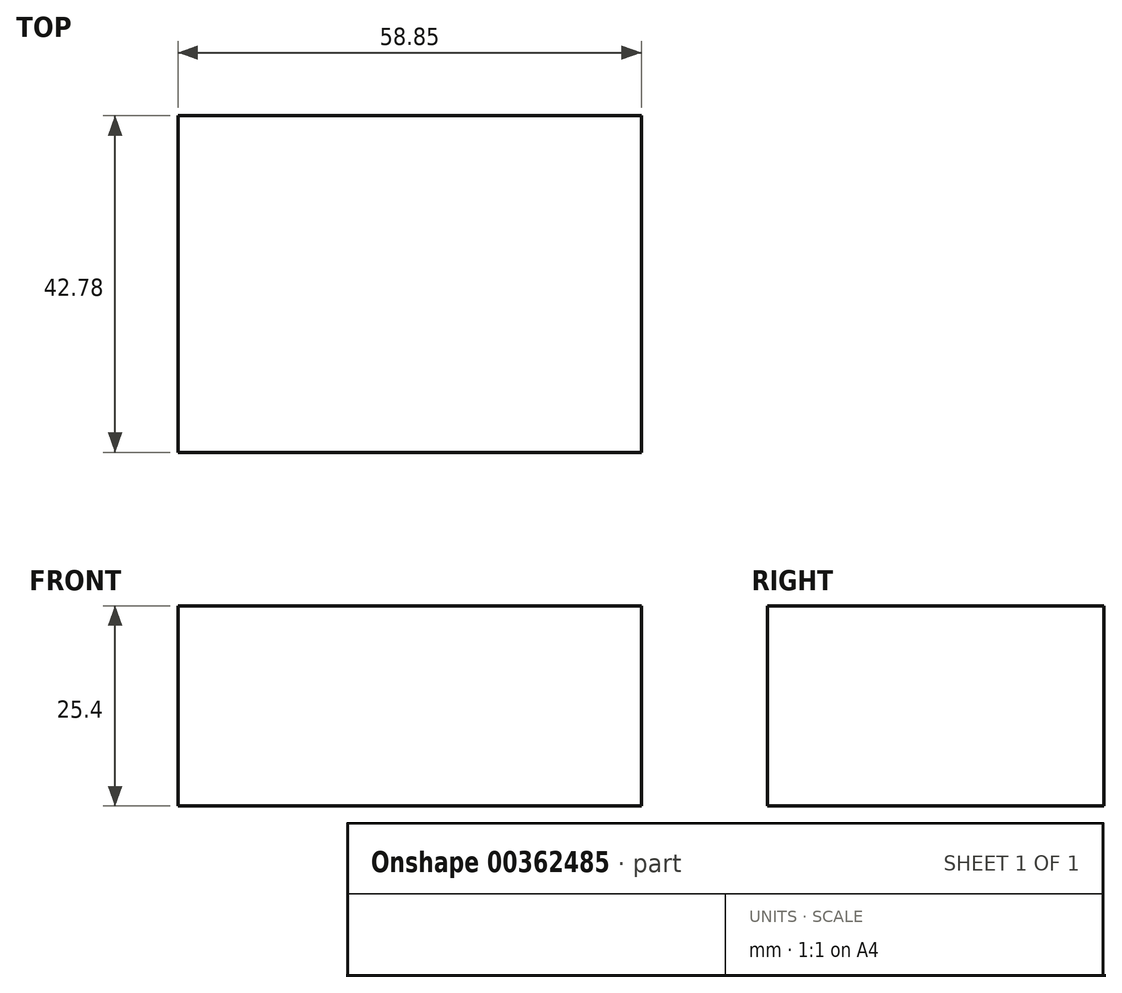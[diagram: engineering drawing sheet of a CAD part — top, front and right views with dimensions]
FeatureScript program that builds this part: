
annotation { "Feature Type Name" : "Feature", "Feature Type Description" : "" }
export const myFeature = defineFeature(function(context is Context, id is Id, definition is map)
    precondition{}
    {
        {
            var Q0;
            Q0=qCreatedBy(makeId("Top.planeOp"),FACE);
            var sketch = newSketch(context, id + "F0", { "sketchPlane" : qUnion([Q0])});
            skLineSegment(sketch, "E0.bottom", {"start": v(64.18, 13.52) * mm, "end": v(5.33, 13.52) * mm});
            skLineSegment(sketch, "E0.top", {"start": v(64.18, 56.3) * mm, "end": v(5.33, 56.3) * mm});
            skLineSegment(sketch, "E0.left", {"start": v(64.18, 13.52) * mm, "end": v(64.18, 56.3) * mm});
            skLineSegment(sketch, "E0.right", {"start": v(5.33, 13.52) * mm, "end": v(5.33, 56.3) * mm});
            skPoint(sketch, "E0.middle", {"position": v(34.75, 34.9) * mm});
            skSolve(sketch);
        }
        {
            var Q0;
            Q0=makeQuery(id+"F0.imprint","IMPRINT",FACE,{"disambiguationData":[TD([[makeQuery(id+"F0.imprint","IMPRINT",EDGE,{"derivedFrom":sQuery(id+"F0.wireOp",EDGE,"E0.bottom")}),-1.0]])]});
            extrude(context, id + "F1", {"entities" : qUnion([Q0]), "depth" : 25.4 * mm});
        }
    });
